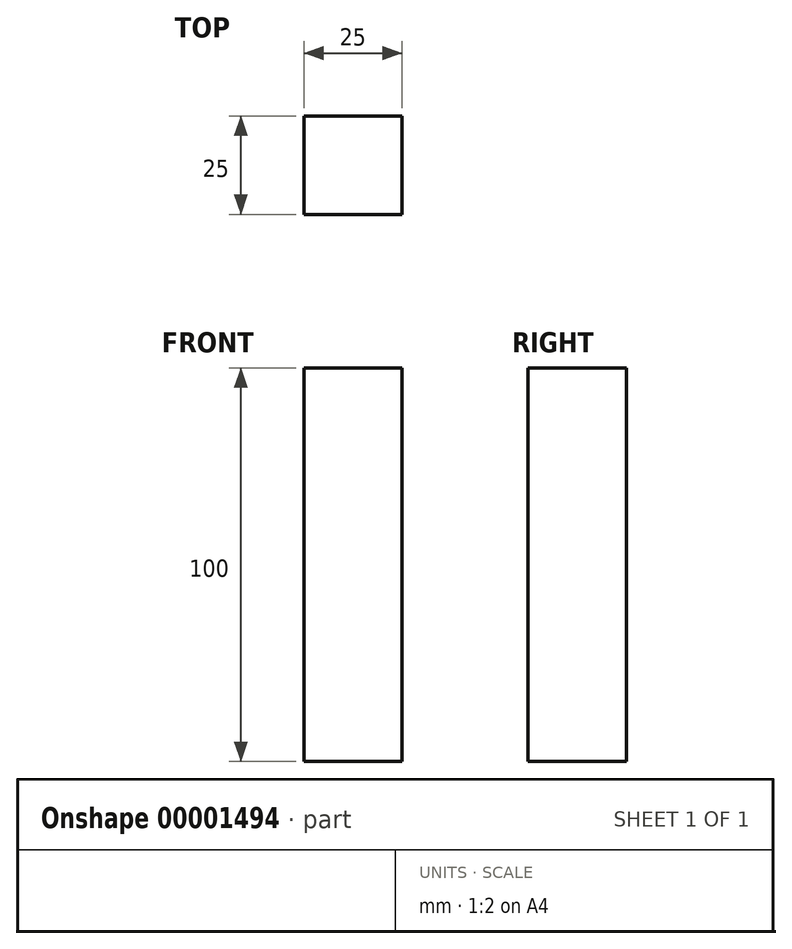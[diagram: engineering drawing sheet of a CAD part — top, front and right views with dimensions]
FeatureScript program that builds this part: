
annotation { "Feature Type Name" : "Feature", "Feature Type Description" : "" }
export const myFeature = defineFeature(function(context is Context, id is Id, definition is map)
    precondition{}
    {
        {
            var Q0;
            Q0=qCreatedBy(makeId("Top.planeOp"),FACE);
            var sketch = newSketch(context, id + "F0", { "sketchPlane" : qUnion([Q0])});
            skLineSegment(sketch, "E0.bottom", {"start": v(-15.35, 10.62) * mm, "end": v(9.65, 10.62) * mm});
            skLineSegment(sketch, "E0.top", {"start": v(-15.35, -14.38) * mm, "end": v(9.65, -14.38) * mm});
            skLineSegment(sketch, "E0.left", {"start": v(-15.35, 10.62) * mm, "end": v(-15.35, -14.38) * mm});
            skLineSegment(sketch, "E0.right", {"start": v(9.65, 10.62) * mm, "end": v(9.65, -14.38) * mm});
            skSolve(sketch);
        }
        {
            var Q0;
            Q0=makeQuery(id+"F0.imprint","IMPRINT",FACE,{"disambiguationData":[TD([[makeQuery(id+"F0.imprint","IMPRINT",EDGE,{"derivedFrom":sQuery(id+"F0.wireOp",EDGE,"E0.bottom")}),-1.0]])]});
            extrude(context, id + "F1", {"entities" : qUnion([Q0]), "depth" : 100 * mm});
        }
    });
